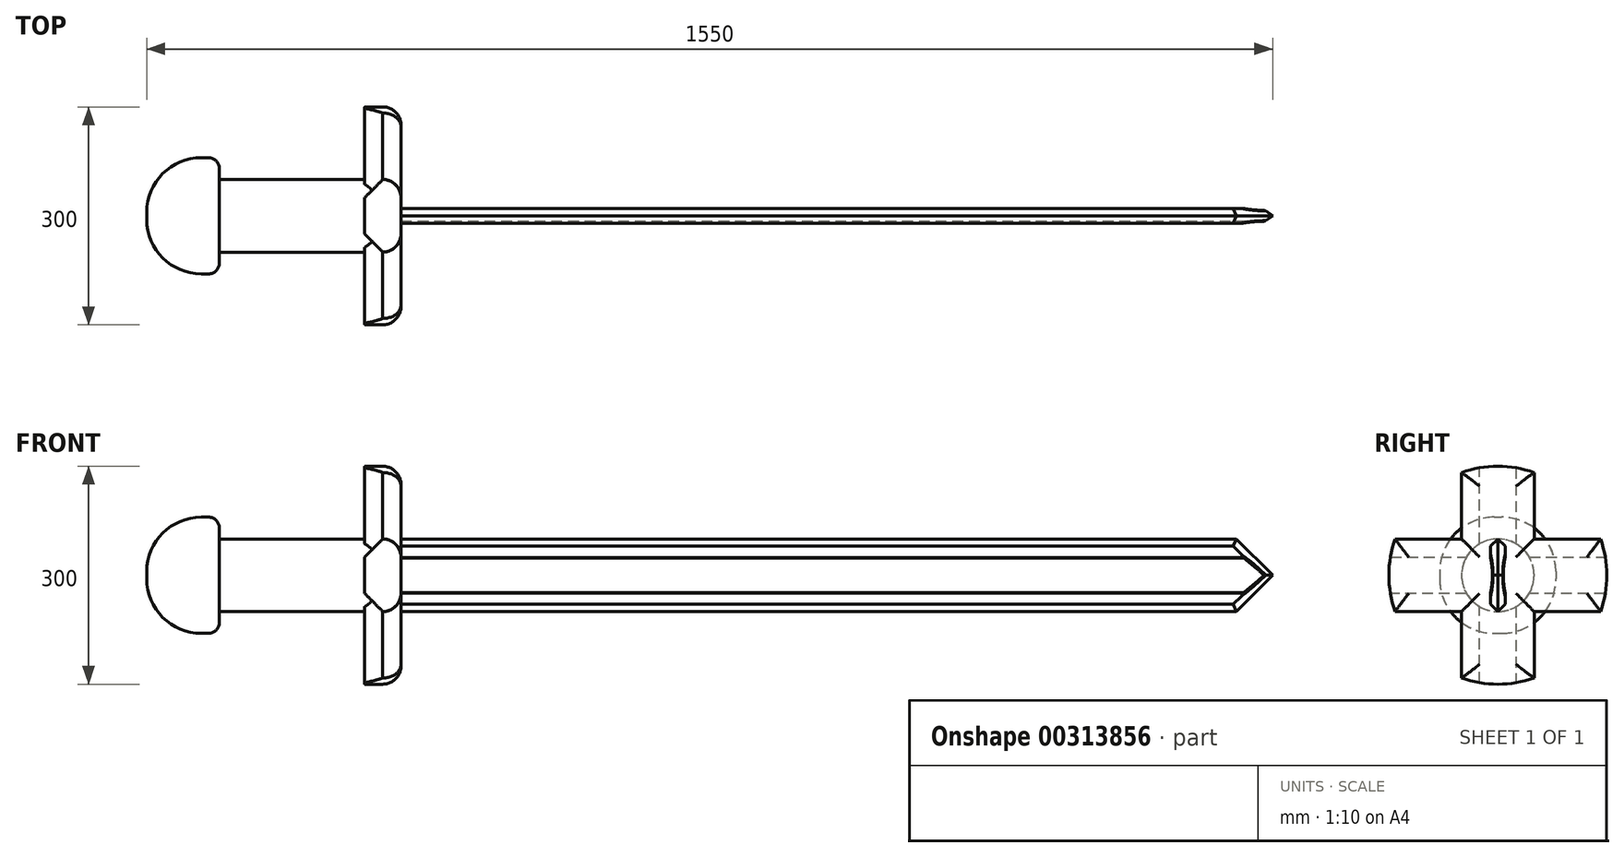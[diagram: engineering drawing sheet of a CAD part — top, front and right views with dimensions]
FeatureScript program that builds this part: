
annotation { "Feature Type Name" : "Feature", "Feature Type Description" : "" }
export const myFeature = defineFeature(function(context is Context, id is Id, definition is map)
    precondition{}
    {
        {
            var Q0;
            Q0=qCreatedBy(makeId("Front.planeOp"),FACE);
            var sketch = newSketch(context, id + "F0", { "sketchPlane" : qUnion([Q0])});
            skLineSegment(sketch, "E0.bottom", {"start": v(0, 50) * mm, "end": v(1200, 50) * mm});
            skLineSegment(sketch, "E0.top", {"start": v(0, -50) * mm, "end": v(1200, -50) * mm});
            skLineSegment(sketch, "E0.left", {"start": v(0, 50) * mm, "end": v(0, -50) * mm});
            skLineSegment(sketch, "E0.right", {"start": v(1200, 50) * mm, "end": v(1200, -50) * mm});
            skPoint(sketch, "E1", {"position": v(0, 0) * mm});
            skLineSegment(sketch, "E2.bottom", {"start": v(-50, 150) * mm, "end": v(0, 150) * mm});
            skLineSegment(sketch, "E2.top", {"start": v(-50, -150) * mm, "end": v(0, -150) * mm});
            skLineSegment(sketch, "E2.left", {"start": v(-50, 150) * mm, "end": v(-50, -150) * mm});
            skLineSegment(sketch, "E2.right", {"start": v(0, 150) * mm, "end": v(0, -150) * mm});
            skLineSegment(sketch, "E3.bottom", {"start": v(-50, 50) * mm, "end": v(-250, 50) * mm});
            skLineSegment(sketch, "E3.top", {"start": v(-50, -50) * mm, "end": v(-250, -50) * mm});
            skLineSegment(sketch, "E3.left", {"start": v(-50, 50) * mm, "end": v(-50, -50) * mm});
            skLineSegment(sketch, "E3.right", {"start": v(-250, 50) * mm, "end": v(-250, -50) * mm});
            skPoint(sketch, "E4", {"position": v(-50, 0) * mm});
            skLineSegment(sketch, "E5.bottom", {"start": v(-350, 80) * mm, "end": v(-250, 80) * mm});
            skLineSegment(sketch, "E5.top", {"start": v(-350, -80) * mm, "end": v(-250, -80) * mm});
            skLineSegment(sketch, "E5.left", {"start": v(-350, 80) * mm, "end": v(-350, -80) * mm});
            skLineSegment(sketch, "E5.right", {"start": v(-250, 80) * mm, "end": v(-250, -80) * mm});
            skPoint(sketch, "E6", {"position": v(-250, 0) * mm});
            skLineSegment(sketch, "E7.bottom", {"start": v(-50, 50) * mm, "end": v(0, 50) * mm});
            skLineSegment(sketch, "E7.top", {"start": v(-50, -50) * mm, "end": v(0, -50) * mm});
            skSolve(sketch);
        }
        {
            var Q0;
            Q0=qCreatedBy(makeId("Right.planeOp"),FACE);
            var sketch = newSketch(context, id + "F1", { "sketchPlane" : qUnion([Q0])});
            skCircle(sketch, "E8", {"center": v(0, 0) * mm, "radius": 150 * mm});
            skCircle(sketch, "E9", {"center": v(125, 0) * mm, "radius": 117.5 * mm});
            skLineSegment(sketch, "E10.bottom", {"start": v(250, 250) * mm, "end": v(-250, 250) * mm});
            skLineSegment(sketch, "E10.top", {"start": v(250, -250) * mm, "end": v(-250, -250) * mm});
            skLineSegment(sketch, "E10.left", {"start": v(250, 250) * mm, "end": v(250, -250) * mm});
            skLineSegment(sketch, "E10.right", {"start": v(-250, 250) * mm, "end": v(-250, -250) * mm});
            skPoint(sketch, "E11", {"position": v(0, 250) * mm});
            skPoint(sketch, "E12", {"position": v(250, 0) * mm});
            skLineSegment(sketch, "E13", {"start": v(250, 250) * mm, "end": v(0, 250) * mm});
            skPoint(sketch, "E14", {"position": v(125, 250) * mm});
            skCircle(sketch, "E15", {"center": v(-125, 0) * mm, "radius": 117.5 * mm});
            skLineSegment(sketch, "E16", {"start": v(0, 250) * mm, "end": v(-250, 250) * mm});
            skPoint(sketch, "E17", {"position": v(-125, 250) * mm});
            skSolve(sketch);
        }
        {
            var Q0;
            Q0=makeQuery(id+"F0.imprint","IMPRINT",FACE,{"disambiguationData":[TD([[makeQuery(id+"F0.imprint","IMPRINT",EDGE,{"derivedFrom":sQuery(id+"F0.wireOp",EDGE,"E0.bottom")}),-1.0]])]});
            extrude(context, id + "F2", {"entities" : qUnion([Q0]), "depth" : 10 * mm, "hasSecondDirection" : true, "secondDirectionOppositeDirection" : true, "secondDirectionDepth" : 10 * mm});
        }
        {
            var Q0;
            {var subQ0=sQuery(id+"F0.wireOp",EDGE,"E2.top");Q0=makeQuery(id+"F0.imprint","IMPRINT",FACE,{"disambiguationData":[TD([[makeQuery(id+"F0.imprint","IMPRINT",EDGE,{"derivedFrom":subQ0}),1.0]])]});}
            var Q1;
            {var subQ0=sQuery(id+"F0.wireOp",EDGE,"E2.bottom");Q1=makeQuery(id+"F0.imprint","IMPRINT",FACE,{"disambiguationData":[TD([[makeQuery(id+"F0.imprint","IMPRINT",EDGE,{"derivedFrom":subQ0}),-1.0]])]});}
            extrude(context, id + "F3", {"entities" : qUnion([Q0, Q1]), "depth" : 50 * mm, "hasSecondDirection" : true, "secondDirectionOppositeDirection" : true, "secondDirectionDepth" : 50 * mm});
        }
        {
            var Q0;
            Q0=makeQuery(id+"F0.imprint","IMPRINT",FACE,{"disambiguationData":[TD([[makeQuery(id+"F0.imprint","IMPRINT",EDGE,{"derivedFrom":sQuery(id+"F0.wireOp",EDGE,"E7.bottom")}),-1.0]])]});
            extrude(context, id + "F4", {"entities" : qUnion([Q0]), "depth" : 150 * mm, "hasSecondDirection" : true, "secondDirectionOppositeDirection" : true, "secondDirectionDepth" : 150 * mm});
        }
        {
            var Q0;
            {var subQ0=sQuery(id+"F0.wireOp",EDGE,"E3.bottom");Q0=makeQuery(id+"F0.imprint","IMPRINT",FACE,{"disambiguationData":[TD([[makeQuery(id+"F0.imprint","IMPRINT",EDGE,{"derivedFrom":subQ0}),1.0]])]});}
            extrude(context, id + "F5", {"entities" : qUnion([Q0]), "operationType" : NewBodyOperationType.ADD, "depth" : 50 * mm, "hasSecondDirection" : true, "secondDirectionOppositeDirection" : true, "secondDirectionDepth" : 50 * mm});
        }
        {
            var Q0;
            {var subQ2=sQuery(id+"F0.wireOp",EDGE,"E5.bottom");Q0=makeQuery(id+"F0.imprint","IMPRINT",FACE,{"disambiguationData":[TD([[makeQuery(id+"F0.imprint","IMPRINT",EDGE,{"derivedFrom":subQ2}),-1.0]])]});}
            extrude(context, id + "F6", {"entities" : qUnion([Q0]), "operationType" : NewBodyOperationType.ADD, "depth" : 80 * mm, "hasSecondDirection" : true, "secondDirectionOppositeDirection" : true, "secondDirectionDepth" : 80 * mm});
        }
        {
            var Q0;
            Q0=makeQuery(id+"F1.imprint","IMPRINT",FACE,{"disambiguationData":[TD([[makeQuery(id+"F1.imprint","IMPRINT",EDGE,{"derivedFrom":sQuery(id+"F1.wireOp",EDGE,"E8")}),-1.0]])]});
            extrude(context, id + "F7", {"entities" : qUnion([Q0]), "operationType" : NewBodyOperationType.REMOVE, "oppositeDirection" : true, "depth" : 50 * mm, "hasSecondDirection" : true, "secondDirectionOppositeDirection" : false, "secondDirectionDepth" : 50 * mm});
        }
        {
            var Q0;
            Q0=makeQuery(id+"F2.opExtrude","SWEPT_EDGE",EDGE,{"disambiguationData":[OSD([sQuery(id+"F0.wireOp",EDGE,"E0.bottom"),sQuery(id+"F0.wireOp",EDGE,"E0.right")])]});
            var Q1;
            Q1=makeQuery(id+"F2.opExtrude","SWEPT_EDGE",EDGE,{"disambiguationData":[OSD([sQuery(id+"F0.wireOp",EDGE,"E0.top"),sQuery(id+"F0.wireOp",EDGE,"E0.right")])]});
            chamfer(context, id + "F8", {"entities" : qUnion([Q0, Q1]), "width" : 50 * mm, "tangentPropagation" : true});
        }
        {
            var Q0;
            Q0=makeQuery(id+"F2.opExtrude","CAP_EDGE",EDGE,{"disambiguationData":[OSD([sQuery(id+"F0.wireOp",EDGE,"E0.bottom")])],"isStart":false});
            var Q1;
            Q1=makeQuery(id+"F2.opExtrude","CAP_EDGE",EDGE,{"disambiguationData":[OSD([sQuery(id+"F0.wireOp",EDGE,"E0.bottom")])],"isStart":true});
            var Q2;
            Q2=makeQuery(id+"F2.opExtrude","CAP_EDGE",EDGE,{"disambiguationData":[OSD([sQuery(id+"F0.wireOp",EDGE,"E0.top")])],"isStart":false});
            var Q3;
            Q3=makeQuery(id+"F2.opExtrude","CAP_EDGE",EDGE,{"disambiguationData":[OSD([sQuery(id+"F0.wireOp",EDGE,"E0.top")])],"isStart":true});
            var Q4;
            {var subQ0=sQuery(id+"F0.wireOp",EDGE,"E0.right");var subQ1=sQuery(id+"F0.wireOp",EDGE,"E0.bottom");Q4=makeQuery(id+"F8.opChamfer","BLEND_EDGE",EDGE,{"blendedFrom":[makeQuery(id+"F2.opExtrude","SWEPT_EDGE",EDGE,{"disambiguationData":[OSD([subQ1,subQ0])]}),makeQuery(id+"F2.opExtrude","CAP_FACE",FACE,{"disambiguationData":[OSD([subQ1,sQuery(id+"F0.wireOp",EDGE,"E0.top"),subQ0,sQuery(id+"F0.wireOp",EDGE,"E0.left")])],"isStart":true})],"blendedInto":[makeQuery(id+"F2.opExtrude","CAP_FACE",FACE,{"disambiguationData":[OSD([subQ1,sQuery(id+"F0.wireOp",EDGE,"E0.top"),subQ0,sQuery(id+"F0.wireOp",EDGE,"E0.left")])],"isStart":true})]});}
            var Q5;
            {var subQ0=sQuery(id+"F0.wireOp",EDGE,"E0.right");var subQ1=sQuery(id+"F0.wireOp",EDGE,"E0.bottom");Q5=makeQuery(id+"F8.opChamfer","BLEND_EDGE",EDGE,{"blendedFrom":[makeQuery(id+"F2.opExtrude","SWEPT_EDGE",EDGE,{"disambiguationData":[OSD([subQ1,subQ0])]}),makeQuery(id+"F2.opExtrude","CAP_FACE",FACE,{"disambiguationData":[OSD([subQ1,sQuery(id+"F0.wireOp",EDGE,"E0.top"),subQ0,sQuery(id+"F0.wireOp",EDGE,"E0.left")])],"isStart":false})],"blendedInto":[makeQuery(id+"F2.opExtrude","CAP_FACE",FACE,{"disambiguationData":[OSD([subQ1,sQuery(id+"F0.wireOp",EDGE,"E0.top"),subQ0,sQuery(id+"F0.wireOp",EDGE,"E0.left")])],"isStart":false})]});}
            var Q6;
            {var subQ0=sQuery(id+"F0.wireOp",EDGE,"E0.right");var subQ1=sQuery(id+"F0.wireOp",EDGE,"E0.top");Q6=makeQuery(id+"F8.opChamfer","BLEND_EDGE",EDGE,{"blendedFrom":[makeQuery(id+"F2.opExtrude","SWEPT_EDGE",EDGE,{"disambiguationData":[OSD([subQ1,subQ0])]}),makeQuery(id+"F2.opExtrude","CAP_FACE",FACE,{"disambiguationData":[OSD([sQuery(id+"F0.wireOp",EDGE,"E0.bottom"),subQ1,subQ0,sQuery(id+"F0.wireOp",EDGE,"E0.left")])],"isStart":true})],"blendedInto":[makeQuery(id+"F2.opExtrude","CAP_FACE",FACE,{"disambiguationData":[OSD([sQuery(id+"F0.wireOp",EDGE,"E0.bottom"),subQ1,subQ0,sQuery(id+"F0.wireOp",EDGE,"E0.left")])],"isStart":true})]});}
            var Q7;
            {var subQ0=sQuery(id+"F0.wireOp",EDGE,"E0.right");var subQ1=sQuery(id+"F0.wireOp",EDGE,"E0.top");Q7=makeQuery(id+"F8.opChamfer","BLEND_EDGE",EDGE,{"blendedFrom":[makeQuery(id+"F2.opExtrude","SWEPT_EDGE",EDGE,{"disambiguationData":[OSD([subQ1,subQ0])]}),makeQuery(id+"F2.opExtrude","CAP_FACE",FACE,{"disambiguationData":[OSD([sQuery(id+"F0.wireOp",EDGE,"E0.bottom"),subQ1,subQ0,sQuery(id+"F0.wireOp",EDGE,"E0.left")])],"isStart":false})],"blendedInto":[makeQuery(id+"F2.opExtrude","CAP_FACE",FACE,{"disambiguationData":[OSD([sQuery(id+"F0.wireOp",EDGE,"E0.bottom"),subQ1,subQ0,sQuery(id+"F0.wireOp",EDGE,"E0.left")])],"isStart":false})]});}
            chamfer(context, id + "F9", {"entities" : qUnion([Q0, Q1, Q2, Q3, Q4, Q5, Q6, Q7]), "width" : 10 * mm, "tangentPropagation" : true});
        }
        {
            var Q0;
            {var subQ0=sQuery(id+"F1.wireOp",EDGE,"E15");var subQ1=sQuery(id+"F1.wireOp",EDGE,"E8");var subQ2=makeQuery(id+"F1.imprint","INTERSECT",VERTEX,{"disambiguationData":[OD(0.0)],"derivedFrom":[subQ1,subQ0]});Q0=makeQuery(id+"F1.imprint","IMPRINT",FACE,{"disambiguationData":[TD([[makeQuery(id+"F1.imprint","IMPRINT",EDGE,{"disambiguationData":[TD([[subQ2,-1.0]])],"derivedFrom":subQ1}),1.0]])]});}
            var Q1;
            {var subQ0=sQuery(id+"F1.wireOp",EDGE,"E9");var subQ1=sQuery(id+"F1.wireOp",EDGE,"E8");var subQ2=makeQuery(id+"F1.imprint","INTERSECT",VERTEX,{"disambiguationData":[OD(0.0)],"derivedFrom":[subQ1,subQ0]});Q1=makeQuery(id+"F1.imprint","IMPRINT",FACE,{"disambiguationData":[TD([[makeQuery(id+"F1.imprint","IMPRINT",EDGE,{"disambiguationData":[TD([[subQ2,1.0]])],"derivedFrom":subQ1}),1.0]])]});}
            extrude(context, id + "F10", {"entities" : qUnion([Q0, Q1]), "operationType" : NewBodyOperationType.REMOVE, "depth" : 1500 * mm});
        }
        {
            var Q0;
            {var subQ0=sQuery(id+"F0.wireOp",EDGE,"E0.left");var subQ1=sQuery(id+"F0.wireOp",EDGE,"E2.right");Q0=makeQuery(id+"F5.boolean.opBoolean","MERGE",FACE,{"derivedFrom":[makeQuery(id+"F3.opExtrude","SWEPT_FACE",FACE,{"disambiguationData":[OSD([subQ1]),TDD([makeQuery(id+"F0.imprint","IMPRINT",EDGE,{"disambiguationData":[TD([[makeQuery(id+"F0.imprint","INTERSECT",VERTEX,{"derivedFrom":[sQuery(id+"F0.wireOp",EDGE,"E2.bottom"),subQ1]}),-1.0]])],"derivedFrom":subQ1})])]}),makeQuery(id+"F3.opExtrude","SWEPT_FACE",FACE,{"disambiguationData":[OSD([subQ1]),TDD([makeQuery(id+"F0.imprint","IMPRINT",EDGE,{"disambiguationData":[TD([[makeQuery(id+"F0.imprint","INTERSECT",VERTEX,{"derivedFrom":[sQuery(id+"F0.wireOp",EDGE,"E2.top"),subQ1]}),1.0]])],"derivedFrom":subQ1})])]}),makeQuery(id+"F4.opExtrude","SWEPT_FACE",FACE,{"disambiguationData":[OSD([subQ0])]})]});}
            fillet(context, id + "F11", {"entities" : qUnion([Q0]), "radius" : 25 * mm, "tangentPropagation" : true, "allowEdgeOverflow" : false});
        }
        {
            var Q0;
            Q0=makeQuery(id+"F5.opExtrude","CAP_EDGE",EDGE,{"disambiguationData":[OSD([sQuery(id+"F0.wireOp",EDGE,"E3.bottom")])],"isStart":false});
            var Q1;
            Q1=makeQuery(id+"F5.opExtrude","CAP_EDGE",EDGE,{"disambiguationData":[OSD([sQuery(id+"F0.wireOp",EDGE,"E3.top")])],"isStart":false});
            var Q2;
            Q2=makeQuery(id+"F5.opExtrude","CAP_EDGE",EDGE,{"disambiguationData":[OSD([sQuery(id+"F0.wireOp",EDGE,"E3.top")])],"isStart":true});
            var Q3;
            Q3=makeQuery(id+"F5.opExtrude","CAP_EDGE",EDGE,{"disambiguationData":[OSD([sQuery(id+"F0.wireOp",EDGE,"E3.bottom")])],"isStart":true});
            fillet(context, id + "F12", {"entities" : qUnion([Q0, Q1, Q2, Q3]), "radius" : 50 * mm, "tangentPropagation" : true, "allowEdgeOverflow" : false});
        }
        {
            var Q0;
            Q0=makeQuery(id+"F6.opExtrude","CAP_EDGE",EDGE,{"disambiguationData":[OSD([sQuery(id+"F0.wireOp",EDGE,"E5.bottom")])],"isStart":false});
            var Q1;
            Q1=makeQuery(id+"F6.opExtrude","CAP_EDGE",EDGE,{"disambiguationData":[OSD([sQuery(id+"F0.wireOp",EDGE,"E5.top")])],"isStart":false});
            var Q2;
            Q2=makeQuery(id+"F6.opExtrude","CAP_EDGE",EDGE,{"disambiguationData":[OSD([sQuery(id+"F0.wireOp",EDGE,"E5.top")])],"isStart":true});
            var Q3;
            Q3=makeQuery(id+"F6.opExtrude","CAP_EDGE",EDGE,{"disambiguationData":[OSD([sQuery(id+"F0.wireOp",EDGE,"E5.bottom")])],"isStart":true});
            fillet(context, id + "F13", {"entities" : qUnion([Q0, Q1, Q2, Q3]), "radius" : 75 * mm, "tangentPropagation" : true, "allowEdgeOverflow" : false});
        }
        {
            var Q0;
            Q0=makeQuery(id+"F13.opFillet","BLEND_EDGE",EDGE,{"blendedFrom":[makeQuery(id+"F6.opExtrude","CAP_EDGE",EDGE,{"disambiguationData":[OSD([sQuery(id+"F0.wireOp",EDGE,"E5.bottom")])],"isStart":true}),makeQuery(id+"F6.opExtrude","SWEPT_FACE",FACE,{"disambiguationData":[OSD([sQuery(id+"F0.wireOp",EDGE,"E5.left")])]})],"blendedInto":[makeQuery(id+"F6.opExtrude","SWEPT_FACE",FACE,{"disambiguationData":[OSD([sQuery(id+"F0.wireOp",EDGE,"E5.left")])]})]});
            var Q1;
            Q1=makeQuery(id+"F13.opFillet","BLEND_EDGE",EDGE,{"blendedFrom":[makeQuery(id+"F6.opExtrude","CAP_EDGE",EDGE,{"disambiguationData":[OSD([sQuery(id+"F0.wireOp",EDGE,"E5.top")])],"isStart":true}),makeQuery(id+"F6.opExtrude","SWEPT_FACE",FACE,{"disambiguationData":[OSD([sQuery(id+"F0.wireOp",EDGE,"E5.left")])]})],"blendedInto":[makeQuery(id+"F6.opExtrude","SWEPT_FACE",FACE,{"disambiguationData":[OSD([sQuery(id+"F0.wireOp",EDGE,"E5.left")])]})]});
            var Q2;
            Q2=makeQuery(id+"F13.opFillet","BLEND_EDGE",EDGE,{"blendedFrom":[makeQuery(id+"F6.opExtrude","CAP_EDGE",EDGE,{"disambiguationData":[OSD([sQuery(id+"F0.wireOp",EDGE,"E5.top")])],"isStart":false}),makeQuery(id+"F6.opExtrude","SWEPT_FACE",FACE,{"disambiguationData":[OSD([sQuery(id+"F0.wireOp",EDGE,"E5.left")])]})],"blendedInto":[makeQuery(id+"F6.opExtrude","SWEPT_FACE",FACE,{"disambiguationData":[OSD([sQuery(id+"F0.wireOp",EDGE,"E5.left")])]})]});
            var Q3;
            Q3=makeQuery(id+"F13.opFillet","BLEND_EDGE",EDGE,{"blendedFrom":[makeQuery(id+"F6.opExtrude","CAP_EDGE",EDGE,{"disambiguationData":[OSD([sQuery(id+"F0.wireOp",EDGE,"E5.bottom")])],"isStart":false}),makeQuery(id+"F6.opExtrude","SWEPT_FACE",FACE,{"disambiguationData":[OSD([sQuery(id+"F0.wireOp",EDGE,"E5.left")])]})],"blendedInto":[makeQuery(id+"F6.opExtrude","SWEPT_FACE",FACE,{"disambiguationData":[OSD([sQuery(id+"F0.wireOp",EDGE,"E5.left")])]})]});
            fillet(context, id + "F14", {"entities" : qUnion([Q0, Q1, Q2, Q3]), "radius" : 75 * mm, "tangentPropagation" : true, "allowEdgeOverflow" : false});
        }
        {
            var Q0;
            Q0=makeQuery(id+"F13.opFillet","BLEND_EDGE",EDGE,{"blendedFrom":[makeQuery(id+"F6.opExtrude","CAP_EDGE",EDGE,{"disambiguationData":[OSD([sQuery(id+"F0.wireOp",EDGE,"E5.bottom")])],"isStart":false}),makeQuery(id+"F6.opExtrude","SWEPT_FACE",FACE,{"disambiguationData":[OSD([sQuery(id+"F0.wireOp",EDGE,"E5.right")])]})],"blendedInto":[makeQuery(id+"F6.opExtrude","SWEPT_FACE",FACE,{"disambiguationData":[OSD([sQuery(id+"F0.wireOp",EDGE,"E5.right")])]})]});
            var Q1;
            Q1=makeQuery(id+"F13.opFillet","BLEND_EDGE",EDGE,{"blendedFrom":[makeQuery(id+"F6.opExtrude","CAP_EDGE",EDGE,{"disambiguationData":[OSD([sQuery(id+"F0.wireOp",EDGE,"E5.top")])],"isStart":false}),makeQuery(id+"F6.opExtrude","SWEPT_FACE",FACE,{"disambiguationData":[OSD([sQuery(id+"F0.wireOp",EDGE,"E5.right")])]})],"blendedInto":[makeQuery(id+"F6.opExtrude","SWEPT_FACE",FACE,{"disambiguationData":[OSD([sQuery(id+"F0.wireOp",EDGE,"E5.right")])]})]});
            var Q2;
            Q2=makeQuery(id+"F13.opFillet","BLEND_EDGE",EDGE,{"blendedFrom":[makeQuery(id+"F6.opExtrude","CAP_EDGE",EDGE,{"disambiguationData":[OSD([sQuery(id+"F0.wireOp",EDGE,"E5.bottom")])],"isStart":true}),makeQuery(id+"F6.opExtrude","SWEPT_FACE",FACE,{"disambiguationData":[OSD([sQuery(id+"F0.wireOp",EDGE,"E5.right")])]})],"blendedInto":[makeQuery(id+"F6.opExtrude","SWEPT_FACE",FACE,{"disambiguationData":[OSD([sQuery(id+"F0.wireOp",EDGE,"E5.right")])]})]});
            var Q3;
            Q3=makeQuery(id+"F13.opFillet","BLEND_EDGE",EDGE,{"blendedFrom":[makeQuery(id+"F6.opExtrude","CAP_EDGE",EDGE,{"disambiguationData":[OSD([sQuery(id+"F0.wireOp",EDGE,"E5.top")])],"isStart":true}),makeQuery(id+"F6.opExtrude","SWEPT_FACE",FACE,{"disambiguationData":[OSD([sQuery(id+"F0.wireOp",EDGE,"E5.right")])]})],"blendedInto":[makeQuery(id+"F6.opExtrude","SWEPT_FACE",FACE,{"disambiguationData":[OSD([sQuery(id+"F0.wireOp",EDGE,"E5.right")])]})]});
            fillet(context, id + "F15", {"entities" : qUnion([Q0, Q1, Q2, Q3]), "radius" : 15 * mm, "tangentPropagation" : true, "allowEdgeOverflow" : false});
        }
        {
            var Q0;
            Q0=makeQuery(id+"F3.opExtrude","SWEPT_EDGE",EDGE,{"disambiguationData":[OSD([sQuery(id+"F0.wireOp",EDGE,"E2.bottom"),sQuery(id+"F0.wireOp",EDGE,"E2.left")])]});
            var Q1;
            {var subQ0=sQuery(id+"F1.wireOp",EDGE,"E9");var subQ1=sQuery(id+"F1.wireOp",EDGE,"E8");Q1=makeQuery(id+"F7.boolean.opBoolean","COPY",EDGE,{"derivedFrom":makeQuery(id+"F7.opExtrude","CAP_EDGE",EDGE,{"disambiguationData":[OSD([subQ1]),TDD([makeQuery(id+"F1.imprint","IMPRINT",EDGE,{"disambiguationData":[TD([[makeQuery(id+"F1.imprint","INTERSECT",VERTEX,{"disambiguationData":[OD(0.0)],"derivedFrom":[subQ1,subQ0]}),1.0]])],"derivedFrom":subQ1})])],"isStart":false})});}
            var Q2;
            Q2=makeQuery(id+"F3.opExtrude","SWEPT_EDGE",EDGE,{"disambiguationData":[OSD([sQuery(id+"F0.wireOp",EDGE,"E2.top"),sQuery(id+"F0.wireOp",EDGE,"E2.left")])]});
            var Q3;
            {var subQ0=sQuery(id+"F1.wireOp",EDGE,"E15");var subQ1=sQuery(id+"F1.wireOp",EDGE,"E8");Q3=makeQuery(id+"F7.boolean.opBoolean","COPY",EDGE,{"derivedFrom":makeQuery(id+"F7.opExtrude","CAP_EDGE",EDGE,{"disambiguationData":[OSD([subQ1]),TDD([makeQuery(id+"F1.imprint","IMPRINT",EDGE,{"disambiguationData":[TD([[makeQuery(id+"F1.imprint","INTERSECT",VERTEX,{"disambiguationData":[OD(0.0)],"derivedFrom":[subQ1,subQ0]}),-1.0]])],"derivedFrom":subQ1})])],"isStart":false})});}
            var Q4;
            {var subQ0=sQuery(id+"F0.wireOp",EDGE,"E3.left");var subQ1=sQuery(id+"F0.wireOp",EDGE,"E7.bottom");var subQ2=sQuery(id+"F0.wireOp",EDGE,"E2.left");var subQ3=sQuery(id+"F0.wireOp",EDGE,"E2.bottom");var subQ4=sQuery(id+"F0.wireOp",EDGE,"E3.bottom");Q4=makeQuery(id+"F5.boolean.opBoolean","SPLIT",EDGE,{"disambiguationData":[TD([makeQuery(id+"F3.opExtrude","CAP_FACE",FACE,{"disambiguationData":[OSD([subQ3,subQ2,sQuery(id+"F0.wireOp",EDGE,"E2.right"),subQ1])],"isStart":false})])],"derivedFrom":makeQuery(id+"F4.opExtrude","SWEPT_EDGE",EDGE,{"disambiguationData":[OSD([subQ2,subQ4,subQ1,subQ0])]})});}
            var Q5;
            {var subQ0=sQuery(id+"F0.wireOp",EDGE,"E2.left");Q5=makeQuery(id+"F3.opExtrude","CAP_EDGE",EDGE,{"disambiguationData":[OSD([subQ0]),TDD([makeQuery(id+"F0.imprint","IMPRINT",EDGE,{"disambiguationData":[TD([[makeQuery(id+"F0.imprint","INTERSECT",VERTEX,{"derivedFrom":[sQuery(id+"F0.wireOp",EDGE,"E2.bottom"),subQ0]}),-1.0]])],"derivedFrom":subQ0})])],"isStart":false});}
            var Q6;
            {var subQ0=sQuery(id+"F0.wireOp",EDGE,"E2.left");Q6=makeQuery(id+"F3.opExtrude","CAP_EDGE",EDGE,{"disambiguationData":[OSD([subQ0]),TDD([makeQuery(id+"F0.imprint","IMPRINT",EDGE,{"disambiguationData":[TD([[makeQuery(id+"F0.imprint","INTERSECT",VERTEX,{"derivedFrom":[sQuery(id+"F0.wireOp",EDGE,"E2.bottom"),subQ0]}),-1.0]])],"derivedFrom":subQ0})])],"isStart":true});}
            var Q7;
            {var subQ0=sQuery(id+"F0.wireOp",EDGE,"E3.left");var subQ1=sQuery(id+"F0.wireOp",EDGE,"E7.bottom");var subQ2=sQuery(id+"F0.wireOp",EDGE,"E2.left");var subQ3=sQuery(id+"F0.wireOp",EDGE,"E2.bottom");var subQ4=sQuery(id+"F0.wireOp",EDGE,"E3.bottom");Q7=makeQuery(id+"F5.boolean.opBoolean","SPLIT",EDGE,{"disambiguationData":[TD([makeQuery(id+"F3.opExtrude","CAP_FACE",FACE,{"disambiguationData":[OSD([subQ3,subQ2,sQuery(id+"F0.wireOp",EDGE,"E2.right"),subQ1])],"isStart":true})])],"derivedFrom":makeQuery(id+"F4.opExtrude","SWEPT_EDGE",EDGE,{"disambiguationData":[OSD([subQ2,subQ4,subQ1,subQ0])]})});}
            var Q8;
            {var subQ0=sQuery(id+"F0.wireOp",EDGE,"E3.left");var subQ1=sQuery(id+"F0.wireOp",EDGE,"E7.top");var subQ2=sQuery(id+"F0.wireOp",EDGE,"E2.left");var subQ3=sQuery(id+"F0.wireOp",EDGE,"E2.top");var subQ4=sQuery(id+"F0.wireOp",EDGE,"E3.top");Q8=makeQuery(id+"F5.boolean.opBoolean","SPLIT",EDGE,{"disambiguationData":[TD([makeQuery(id+"F3.opExtrude","CAP_FACE",FACE,{"disambiguationData":[OSD([subQ3,subQ2,sQuery(id+"F0.wireOp",EDGE,"E2.right"),subQ1])],"isStart":true})])],"derivedFrom":makeQuery(id+"F4.opExtrude","SWEPT_EDGE",EDGE,{"disambiguationData":[OSD([subQ2,subQ4,subQ1,subQ0])]})});}
            var Q9;
            {var subQ0=sQuery(id+"F0.wireOp",EDGE,"E2.left");Q9=makeQuery(id+"F3.opExtrude","CAP_EDGE",EDGE,{"disambiguationData":[OSD([subQ0]),TDD([makeQuery(id+"F0.imprint","IMPRINT",EDGE,{"disambiguationData":[TD([[makeQuery(id+"F0.imprint","INTERSECT",VERTEX,{"derivedFrom":[sQuery(id+"F0.wireOp",EDGE,"E2.top"),subQ0]}),1.0]])],"derivedFrom":subQ0})])],"isStart":true});}
            var Q10;
            {var subQ0=sQuery(id+"F0.wireOp",EDGE,"E2.left");Q10=makeQuery(id+"F3.opExtrude","CAP_EDGE",EDGE,{"disambiguationData":[OSD([subQ0]),TDD([makeQuery(id+"F0.imprint","IMPRINT",EDGE,{"disambiguationData":[TD([[makeQuery(id+"F0.imprint","INTERSECT",VERTEX,{"derivedFrom":[sQuery(id+"F0.wireOp",EDGE,"E2.top"),subQ0]}),1.0]])],"derivedFrom":subQ0})])],"isStart":false});}
            var Q11;
            {var subQ0=sQuery(id+"F0.wireOp",EDGE,"E7.top");var subQ1=sQuery(id+"F0.wireOp",EDGE,"E2.left");var subQ2=sQuery(id+"F0.wireOp",EDGE,"E2.top");var subQ3=sQuery(id+"F0.wireOp",EDGE,"E3.left");var subQ4=sQuery(id+"F0.wireOp",EDGE,"E3.top");Q11=makeQuery(id+"F5.boolean.opBoolean","SPLIT",EDGE,{"disambiguationData":[TD([makeQuery(id+"F3.opExtrude","CAP_FACE",FACE,{"disambiguationData":[OSD([subQ2,subQ1,sQuery(id+"F0.wireOp",EDGE,"E2.right"),subQ0])],"isStart":false})])],"derivedFrom":makeQuery(id+"F4.opExtrude","SWEPT_EDGE",EDGE,{"disambiguationData":[OSD([subQ1,subQ4,subQ0,subQ3])]})});}
            chamfer(context, id + "F16", {"entities" : qUnion([Q0, Q1, Q2, Q3, Q4, Q5, Q6, Q7, Q8, Q9, Q10, Q11]), "width" : 25 * mm, "tangentPropagation" : true});
        }
        {
            var Q0;
            Q0=makeQuery(id+"F10.boolean.opBoolean","INTERSECT",EDGE,{"disambiguationData":[OD(1.0)],"derivedFrom":[makeQuery(id+"F2.opExtrude","CAP_FACE",FACE,{"disambiguationData":[OSD([sQuery(id+"F0.wireOp",EDGE,"E0.bottom"),sQuery(id+"F0.wireOp",EDGE,"E0.top"),sQuery(id+"F0.wireOp",EDGE,"E0.right"),sQuery(id+"F0.wireOp",EDGE,"E0.left")])],"isStart":false}),makeQuery(id+"F10.opExtrude","SWEPT_FACE",FACE,{"disambiguationData":[OSD([sQuery(id+"F1.wireOp",EDGE,"E15")])]})]});
            var Q1;
            {var subQ0=sQuery(id+"F0.wireOp",EDGE,"E0.left");var subQ1=sQuery(id+"F0.wireOp",EDGE,"E0.right");var subQ2=sQuery(id+"F0.wireOp",EDGE,"E0.top");var subQ3=sQuery(id+"F0.wireOp",EDGE,"E0.bottom");Q1=makeQuery(id+"F10.boolean.opBoolean","INTERSECT",EDGE,{"derivedFrom":[makeQuery(id+"F9.opChamfer","BLEND_FACE",FACE,{"disambiguationData":[OSD([subQ3,subQ2,subQ1,subQ0]),TDD([makeQuery(id+"F8.opChamfer","BLEND_EDGE",EDGE,{"blendedFrom":[makeQuery(id+"F2.opExtrude","SWEPT_EDGE",EDGE,{"disambiguationData":[OSD([subQ2,subQ1])]}),makeQuery(id+"F2.opExtrude","CAP_FACE",FACE,{"disambiguationData":[OSD([subQ3,subQ2,subQ1,subQ0])],"isStart":false})],"blendedInto":[makeQuery(id+"F2.opExtrude","CAP_FACE",FACE,{"disambiguationData":[OSD([subQ3,subQ2,subQ1,subQ0])],"isStart":false})]})])]}),makeQuery(id+"F10.opExtrude","SWEPT_FACE",FACE,{"disambiguationData":[OSD([sQuery(id+"F1.wireOp",EDGE,"E15")])]})]});}
            var Q2;
            {var subQ0=sQuery(id+"F0.wireOp",EDGE,"E0.left");var subQ1=sQuery(id+"F0.wireOp",EDGE,"E0.right");var subQ2=sQuery(id+"F0.wireOp",EDGE,"E0.top");var subQ3=sQuery(id+"F0.wireOp",EDGE,"E0.bottom");Q2=makeQuery(id+"F10.boolean.opBoolean","INTERSECT",EDGE,{"derivedFrom":[makeQuery(id+"F9.opChamfer","BLEND_FACE",FACE,{"disambiguationData":[OSD([subQ3,subQ2,subQ1,subQ0]),TDD([makeQuery(id+"F8.opChamfer","BLEND_EDGE",EDGE,{"blendedFrom":[makeQuery(id+"F2.opExtrude","SWEPT_EDGE",EDGE,{"disambiguationData":[OSD([subQ3,subQ1])]}),makeQuery(id+"F2.opExtrude","CAP_FACE",FACE,{"disambiguationData":[OSD([subQ3,subQ2,subQ1,subQ0])],"isStart":false})],"blendedInto":[makeQuery(id+"F2.opExtrude","CAP_FACE",FACE,{"disambiguationData":[OSD([subQ3,subQ2,subQ1,subQ0])],"isStart":false})]})])]}),makeQuery(id+"F10.opExtrude","SWEPT_FACE",FACE,{"disambiguationData":[OSD([sQuery(id+"F1.wireOp",EDGE,"E15")])]})]});}
            var Q3;
            Q3=makeQuery(id+"F10.boolean.opBoolean","INTERSECT",EDGE,{"disambiguationData":[OD(1.0)],"derivedFrom":[makeQuery(id+"F2.opExtrude","CAP_FACE",FACE,{"disambiguationData":[OSD([sQuery(id+"F0.wireOp",EDGE,"E0.bottom"),sQuery(id+"F0.wireOp",EDGE,"E0.top"),sQuery(id+"F0.wireOp",EDGE,"E0.right"),sQuery(id+"F0.wireOp",EDGE,"E0.left")])],"isStart":true}),makeQuery(id+"F10.opExtrude","SWEPT_FACE",FACE,{"disambiguationData":[OSD([sQuery(id+"F1.wireOp",EDGE,"E9")])]})]});
            var Q4;
            Q4=makeQuery(id+"F10.boolean.opBoolean","INTERSECT",EDGE,{"disambiguationData":[OD(0.0)],"derivedFrom":[makeQuery(id+"F2.opExtrude","CAP_FACE",FACE,{"disambiguationData":[OSD([sQuery(id+"F0.wireOp",EDGE,"E0.bottom"),sQuery(id+"F0.wireOp",EDGE,"E0.top"),sQuery(id+"F0.wireOp",EDGE,"E0.right"),sQuery(id+"F0.wireOp",EDGE,"E0.left")])],"isStart":true}),makeQuery(id+"F10.opExtrude","SWEPT_FACE",FACE,{"disambiguationData":[OSD([sQuery(id+"F1.wireOp",EDGE,"E9")])]})]});
            var Q5;
            {var subQ0=sQuery(id+"F0.wireOp",EDGE,"E0.left");var subQ1=sQuery(id+"F0.wireOp",EDGE,"E0.right");var subQ2=sQuery(id+"F0.wireOp",EDGE,"E0.top");var subQ3=sQuery(id+"F0.wireOp",EDGE,"E0.bottom");Q5=makeQuery(id+"F10.boolean.opBoolean","INTERSECT",EDGE,{"derivedFrom":[makeQuery(id+"F9.opChamfer","BLEND_FACE",FACE,{"disambiguationData":[OSD([subQ3,subQ2,subQ1,subQ0]),TDD([makeQuery(id+"F8.opChamfer","BLEND_EDGE",EDGE,{"blendedFrom":[makeQuery(id+"F2.opExtrude","SWEPT_EDGE",EDGE,{"disambiguationData":[OSD([subQ3,subQ1])]}),makeQuery(id+"F2.opExtrude","CAP_FACE",FACE,{"disambiguationData":[OSD([subQ3,subQ2,subQ1,subQ0])],"isStart":true})],"blendedInto":[makeQuery(id+"F2.opExtrude","CAP_FACE",FACE,{"disambiguationData":[OSD([subQ3,subQ2,subQ1,subQ0])],"isStart":true})]})])]}),makeQuery(id+"F10.opExtrude","SWEPT_FACE",FACE,{"disambiguationData":[OSD([sQuery(id+"F1.wireOp",EDGE,"E9")])]})]});}
            var Q6;
            {var subQ0=sQuery(id+"F0.wireOp",EDGE,"E0.left");var subQ1=sQuery(id+"F0.wireOp",EDGE,"E0.right");var subQ2=sQuery(id+"F0.wireOp",EDGE,"E0.top");var subQ3=sQuery(id+"F0.wireOp",EDGE,"E0.bottom");Q6=makeQuery(id+"F10.boolean.opBoolean","INTERSECT",EDGE,{"derivedFrom":[makeQuery(id+"F9.opChamfer","BLEND_FACE",FACE,{"disambiguationData":[OSD([subQ3,subQ2,subQ1,subQ0]),TDD([makeQuery(id+"F8.opChamfer","BLEND_EDGE",EDGE,{"blendedFrom":[makeQuery(id+"F2.opExtrude","SWEPT_EDGE",EDGE,{"disambiguationData":[OSD([subQ2,subQ1])]}),makeQuery(id+"F2.opExtrude","CAP_FACE",FACE,{"disambiguationData":[OSD([subQ3,subQ2,subQ1,subQ0])],"isStart":true})],"blendedInto":[makeQuery(id+"F2.opExtrude","CAP_FACE",FACE,{"disambiguationData":[OSD([subQ3,subQ2,subQ1,subQ0])],"isStart":true})]})])]}),makeQuery(id+"F10.opExtrude","SWEPT_FACE",FACE,{"disambiguationData":[OSD([sQuery(id+"F1.wireOp",EDGE,"E9")])]})]});}
            var Q7;
            Q7=makeQuery(id+"F10.boolean.opBoolean","INTERSECT",EDGE,{"disambiguationData":[OD(0.0)],"derivedFrom":[makeQuery(id+"F2.opExtrude","CAP_FACE",FACE,{"disambiguationData":[OSD([sQuery(id+"F0.wireOp",EDGE,"E0.bottom"),sQuery(id+"F0.wireOp",EDGE,"E0.top"),sQuery(id+"F0.wireOp",EDGE,"E0.right"),sQuery(id+"F0.wireOp",EDGE,"E0.left")])],"isStart":false}),makeQuery(id+"F10.opExtrude","SWEPT_FACE",FACE,{"disambiguationData":[OSD([sQuery(id+"F1.wireOp",EDGE,"E15")])]})]});
            chamfer(context, id + "F17", {"entities" : qUnion([Q0, Q1, Q2, Q3, Q4, Q5, Q6, Q7]), "width" : 2.5 * mm, "tangentPropagation" : true});
        }
    });
